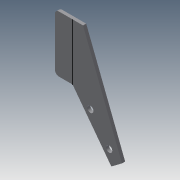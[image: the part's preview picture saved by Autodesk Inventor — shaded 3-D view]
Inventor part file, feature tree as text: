
AUTODESK INVENTOR PART (.ipt)
format: ipt  version: 2013 (Build 170138000, 138)  size: 191,488 bytes
history: native  units: mm
features: sketch x19, extrude x11, fillet x4
ambient origin geometry x8: Origin, YZ Plane, XZ Plane, XY Plane, X Axis, Y Axis, Z Axis, Center Point
bodies: Solid1 (feature_tree)
feature tree (34):
  sketch  "Sketch1"  dims[d4=3.0mm d5=3.0mm d6=2.0mm d7=0.0mm]
  extrude  "Extrusion1"  Depth=2.0mm TaperAngle=0.0deg
  extrude  "Extrusion2"  Depth=2.0mm TaperAngle=0.0deg
  extrude  "Extrusion3"  Depth=2.0mm TaperAngle=0.0deg
  sketch  "Sketch5"  dims[d19=0.5mm d20=0.0mm d21=10.0mm]
  extrude  "Extrusion4"  Depth=6.0mm TaperAngle=0.0deg
  sketch  "Sketch7"  dims[d25=1.5mm d26=0.0mm d27=10.0mm d28=0.0mm]
  sketch  "Sketch8"  dims[d29=2.0mm d30=2.0mm d31=10.0mm d32=0.0mm d33=6.5mm d34=0.0mm]
  extrude  "Extrusion5"  Depth=10.0mm
  sketch  "Sketch10"  dims[d39=2.0mm]
  extrude  "Extrusion6"  Depth=1.5mm TaperAngle=0.0deg
  extrude  "Extrusion7"  Depth=10.0mm TaperAngle=0.0deg
  extrude  "Extrusion8"  Depth=2.0mm
  fillet  "Fillet1"  Radius=10.0mm
  fillet  "Fillet2"  Radius=6.5mm
  sketch  "Sketch14"
  extrude  "Extrusion9"  Depth=2.0mm
  extrude  "Extrusion10"  [1 undecoded]
  sketch  "Sketch17"
  sketch  "Sketch18"
  extrude  "Extrusion11"  [1 undecoded]
  fillet  "Fillet3"  [1 undecoded]
  fillet  "Fillet4"  [1 undecoded]
  sketch  "Sketch2"  dims[d8=10.0mm d11=2.0mm d12=0.0mm]
  sketch  "Sketch3"  dims[d13=5.0mm d14=2.0mm d15=0.0mm]
  sketch  "Sketch4"  dims[d16=2.0mm d17=6.0mm d18=0.0mm]
  sketch  "Sketch6"  dims[d22=5.0mm d23=1.5mm d24=0.0mm]
  sketch  "Sketch9"  dims[d36=2.0mm d37=0.0mm d38=2.0mm]
  sketch  "Sketch11"
  sketch  "Sketch12"
  sketch  "Sketch13"
  sketch  "Sketch15"
  sketch  "Sketch16"
  sketch  "Sketch19"
note: 4 required parameter values undecoded (feature->parameter linkage not recoverable at this tier; creation-order binding heuristic only, values carry confidence <= 0.55)
